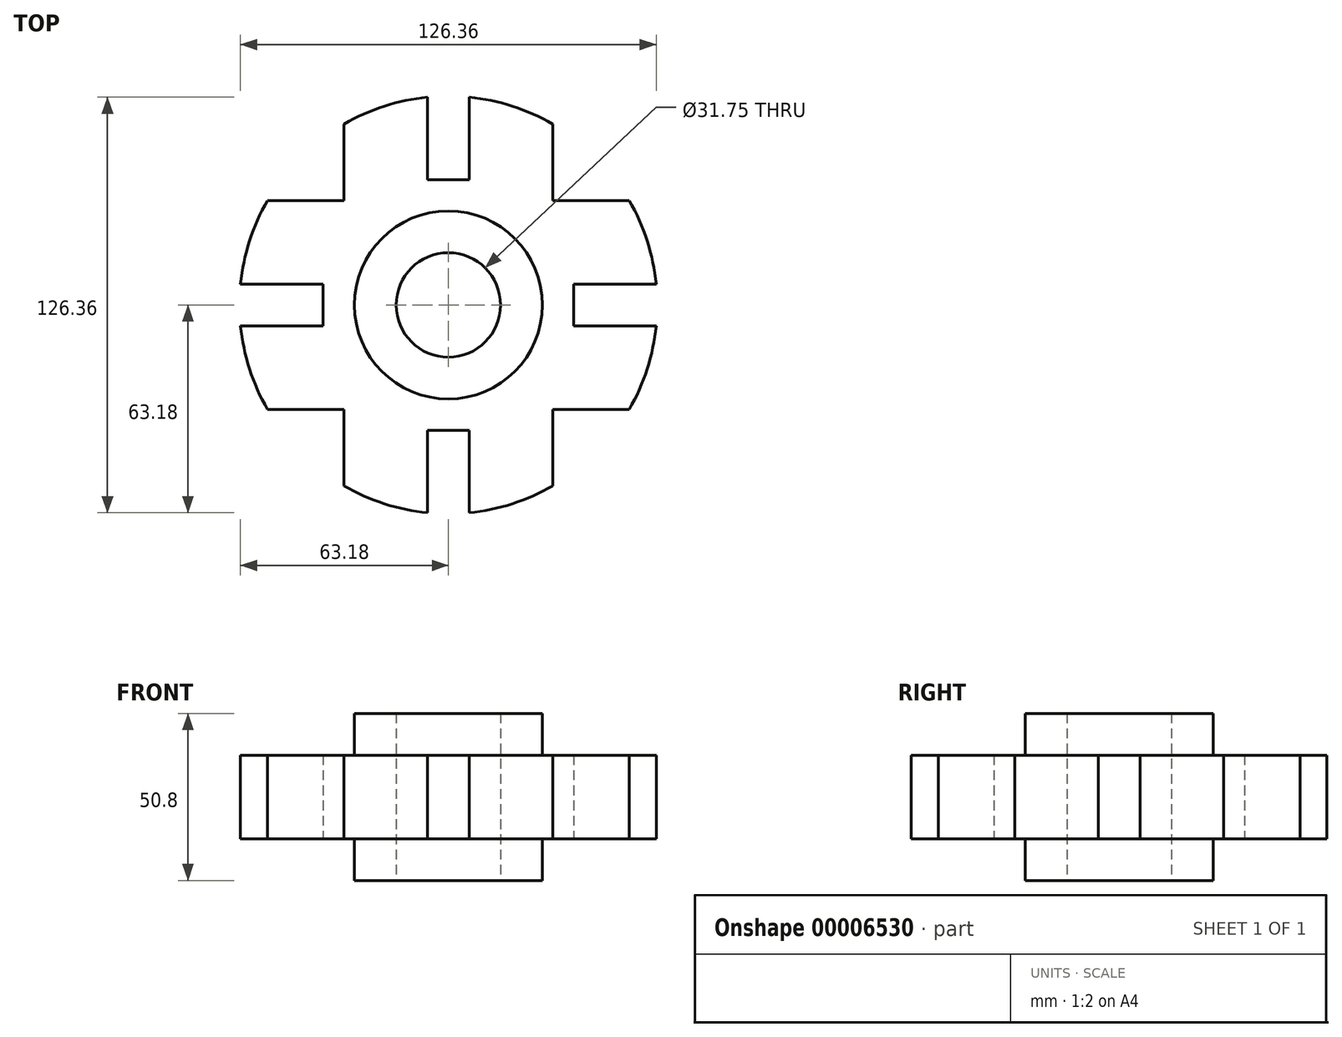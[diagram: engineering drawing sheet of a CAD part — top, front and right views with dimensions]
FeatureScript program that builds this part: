
annotation { "Feature Type Name" : "Feature", "Feature Type Description" : "" }
export const myFeature = defineFeature(function(context is Context, id is Id, definition is map)
    precondition{}
    {
        {
            var Q0;
            Q0=qCreatedBy(makeId("Top.planeOp"),FACE);
            var sketch = newSketch(context, id + "F0", { "sketchPlane" : qUnion([Q0])});
            skCircle(sketch, "E0", {"center": v(0, 0) * mm, "radius": 15.88 * mm});
            skCircle(sketch, "E1", {"center": v(0, 0) * mm, "radius": 28.58 * mm});
            skArc(sketch, "E2", {"start": v(-55, 31.75) * mm, "mid": v(-60.44, 19.49) * mm, "end": v(-63.18, 6.35) * mm});
            skLineSegment(sketch, "E3", {"start": v(-6.35, 63.18) * mm, "end": v(-6.35, 38.1) * mm});
            skLineSegment(sketch, "E4", {"start": v(6.35, -63.18) * mm, "end": v(6.35, -38.1) * mm});
            skLineSegment(sketch, "E5", {"start": v(31.75, 55) * mm, "end": v(31.75, -55) * mm});
            skLineSegment(sketch, "E6", {"start": v(-31.75, -55) * mm, "end": v(-31.75, -31.75) * mm});
            skLineSegment(sketch, "E7.1.0", {"start": v(-55, 31.75) * mm, "end": v(-31.75, 31.75) * mm});
            skLineSegment(sketch, "E7.1.1", {"start": v(63.18, 6.35) * mm, "end": v(31.75, 6.35) * mm});
            skLineSegment(sketch, "E7.1.2", {"start": v(-63.18, -6.35) * mm, "end": v(-38.1, -6.35) * mm});
            skLineSegment(sketch, "E7.1.3", {"start": v(55, -31.75) * mm, "end": v(-55, -31.75) * mm});
            skLineSegment(sketch, "E7.anchor1", {"start": v(0, 0) * mm, "end": v(-31.75, -55) * mm, "construction": true});
            skLineSegment(sketch, "E7.anchor2", {"start": v(0, 0) * mm, "end": v(-55, 31.75) * mm, "construction": true});
            skLineSegment(sketch, "E8", {"start": v(0, 38.1) * mm, "end": v(0, -38.1) * mm, "construction": true});
            skLineSegment(sketch, "E9", {"start": v(6.35, 38.1) * mm, "end": v(-6.35, 38.1) * mm});
            skLineSegment(sketch, "E10", {"start": v(0, -38.1) * mm, "end": v(6.35, -38.1) * mm});
            skLineSegment(sketch, "E11", {"start": v(6.35, -38.1) * mm, "end": v(-6.35, -38.1) * mm});
            skLineSegment(sketch, "E12.1.0", {"start": v(38.1, -6.35) * mm, "end": v(38.1, 6.35) * mm});
            skLineSegment(sketch, "E12.1.1", {"start": v(-38.1, -6.35) * mm, "end": v(-38.1, 6.35) * mm});
            skLineSegment(sketch, "E12.anchor1", {"start": v(0, 0) * mm, "end": v(-6.35, 38.1) * mm, "construction": true});
            skLineSegment(sketch, "E12.anchor2", {"start": v(0, 0) * mm, "end": v(31.75, 5.3) * mm, "construction": true});
            skLineSegment(sketch, "E13.trimOffspring", {"start": v(-31.75, 31.75) * mm, "end": v(-31.75, 55) * mm});
            skLineSegment(sketch, "E14.trimOffspring", {"start": v(31.75, 31.75) * mm, "end": v(55, 31.75) * mm});
            skArc(sketch, "E15.trimOffspring", {"start": v(31.75, 55) * mm, "mid": v(19.49, 60.44) * mm, "end": v(6.35, 63.18) * mm});
            skArc(sketch, "E16.trimOffspring", {"start": v(55, -31.75) * mm, "mid": v(60.44, -19.49) * mm, "end": v(63.18, -6.35) * mm});
            skArc(sketch, "E17.trimOffspring", {"start": v(-31.75, -55) * mm, "mid": v(-19.49, -60.44) * mm, "end": v(-6.35, -63.18) * mm});
            skLineSegment(sketch, "E18.trimOffspring", {"start": v(-27.86, 6.35) * mm, "end": v(-63.18, 6.35) * mm});
            skLineSegment(sketch, "E19.trimOffspring", {"start": v(-6.35, -38.1) * mm, "end": v(-6.35, -63.18) * mm});
            skLineSegment(sketch, "E20.trimOffspring", {"start": v(38.1, -6.35) * mm, "end": v(63.18, -6.35) * mm});
            skArc(sketch, "E21.trimOffspring", {"start": v(-6.35, 63.18) * mm, "mid": v(-19.49, 60.44) * mm, "end": v(-31.75, 55) * mm});
            skArc(sketch, "E22.trimOffspring", {"start": v(63.18, 6.35) * mm, "mid": v(60.44, 19.49) * mm, "end": v(55, 31.75) * mm});
            skArc(sketch, "E23.trimOffspring", {"start": v(-63.18, -6.35) * mm, "mid": v(-60.44, -19.49) * mm, "end": v(-55, -31.75) * mm});
            skArc(sketch, "E24.trimOffspring", {"start": v(6.35, -63.18) * mm, "mid": v(19.49, -60.44) * mm, "end": v(31.75, -55) * mm});
            skLineSegment(sketch, "E25.trimOffspring", {"start": v(6.35, 38.1) * mm, "end": v(6.35, 63.18) * mm});
            skSolve(sketch);
        }
        {
            var Q0;
            {var subQ4=sQuery(id+"F0.wireOp",EDGE,"E1");Q0=makeQuery(id+"F0.imprint","IMPRINT",FACE,{"disambiguationData":[TD([[makeQuery(id+"F0.imprint","IMPRINT",EDGE,{"derivedFrom":subQ4}),-1.0]])]});}
            var Q1;
            {var subQ3=sQuery(id+"F0.wireOp",EDGE,"E4");Q1=makeQuery(id+"F0.imprint","IMPRINT",FACE,{"disambiguationData":[TD([[makeQuery(id+"F0.imprint","IMPRINT",EDGE,{"derivedFrom":subQ3}),-1.0]])]});}
            var Q2;
            {var subQ4=sQuery(id+"F0.wireOp",EDGE,"E12.1.0");Q2=makeQuery(id+"F0.imprint","IMPRINT",FACE,{"disambiguationData":[TD([[makeQuery(id+"F0.imprint","IMPRINT",EDGE,{"derivedFrom":subQ4}),1.0]])]});}
            var Q3;
            {var subQ1=sQuery(id+"F0.wireOp",EDGE,"E14.trimOffspring");Q3=makeQuery(id+"F0.imprint","IMPRINT",FACE,{"disambiguationData":[TD([[makeQuery(id+"F0.imprint","IMPRINT",EDGE,{"derivedFrom":subQ1}),-1.0]])]});}
            extrude(context, id + "F1", {"entities" : qUnion([Q0, Q1, Q2, Q3]), "endBound" : BoundingType.SYMMETRIC, "depth" : 25.4 * mm});
        }
        {
            var Q0;
            Q0=makeQuery(id+"F0.imprint","IMPRINT",FACE,{"disambiguationData":[TD([[makeQuery(id+"F0.imprint","IMPRINT",EDGE,{"derivedFrom":sQuery(id+"F0.wireOp",EDGE,"E0")}),-1.0]])]});
            extrude(context, id + "F2", {"entities" : qUnion([Q0]), "operationType" : NewBodyOperationType.ADD, "endBound" : BoundingType.SYMMETRIC, "depth" : 50.8 * mm});
        }
    });
